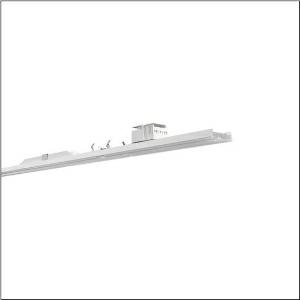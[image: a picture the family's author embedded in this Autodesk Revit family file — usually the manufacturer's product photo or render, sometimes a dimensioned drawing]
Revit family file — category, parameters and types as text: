
# Revit family: licross_r__11_recessed_ho_51tl12cn4cxl_c6f7
name_source: partatom
category: Lighting Fixtures
units: mm (PartAtom-declared; Revit-internal decimal feet)

## family parameters
Cut with Voids When Loaded = No
Host = Face
Light Source = No
Part Type = Normal
Room Calculation Point = No
Round Connector Dimension = Use Diameter
Shared = No

## types (1)
- --- (1 x LED, 12160 lm, 68.8 W, 4000K)
    Apparent Load = 69 VA
    CIE Flux Codes = 66 91 98 100 100
    Color Rendering = 80
    Color Temperature = 4000K
    Default Elevation = 1800 mm
    Description = Licross® 11 Recessed HOluminaire insert, length: 1.500mm, width: 66mm, height: 67mm, LED rated luminous flux: 12.160lm, light colour: 840, control gear: ON/OFF Multilumen, CLOi, control gear: ECG Multilumen, with plug, 3-pole, with phase selection, mains connection: 220..240V, AC, 50/60Hz, halogen-free wiring, primary optical cover: cover, of PMMA, light emission: direct distribution, protection rating (complete): IP40, insulation class (complete): insulation class I (protective earthing), certification: CE, ENEC, VDE, protection symbol: D if used in an environment without relevant dust loads with corresponding accessories, permissible ambient temperature for indoor applications: -35..+35°C, reducing of maximum allowable ambient temperature of 5°C with ceiling mounting, corresponds to IFS (International Featured Standards) requirements for safety and quality in the food industry, packaging unit: 1 piece
    Height = 58 mm
    Lamp = 1 x LED
    Lamp Light Flux = 12160 lm
    Lamp Power = 68.8 W
    Lamp count = 1
    Length = 1500 mm
    Luminous efficacy = 177 lm/W
    Manufacturer = Siteco
    ModVariant = No
    Model = 51TL12CN4CXL
    Mounting Place = Ceiling
    Mounting Type = Pendant
    Number of Poles = 1
    OnlyDefault = Yes
    Power Factor = 1
    Product Name = Licross® 11 Recessed HO
    Product group = luminaire insert
    ProductGroupID = 902
    Protection Class = Protection class I
    Protection Degree = IP 40
    RLX_Detail_Level = 1
    RlxData = <blob elided: 20073 chars, md5=0b26a46e>
    Socket = socket
    Standby Power = 0 W
    System Light Flux = 12160 lm
    System Power = 69 W
    Type Comments = factory setting: luminous flux: 100 % | (A | C | E) | 160 mA
    Type Image = l_1266722.jpg
    URL = http://relux.com
    VarID = @adj_138847
    Voltage = 0 V
    Weight = 0.00 kg
    Width = 66 mm

## geometry (parser evidence)
native form markers: Blend x4, Sweep x11
no freeform markers — native parametric forms only
